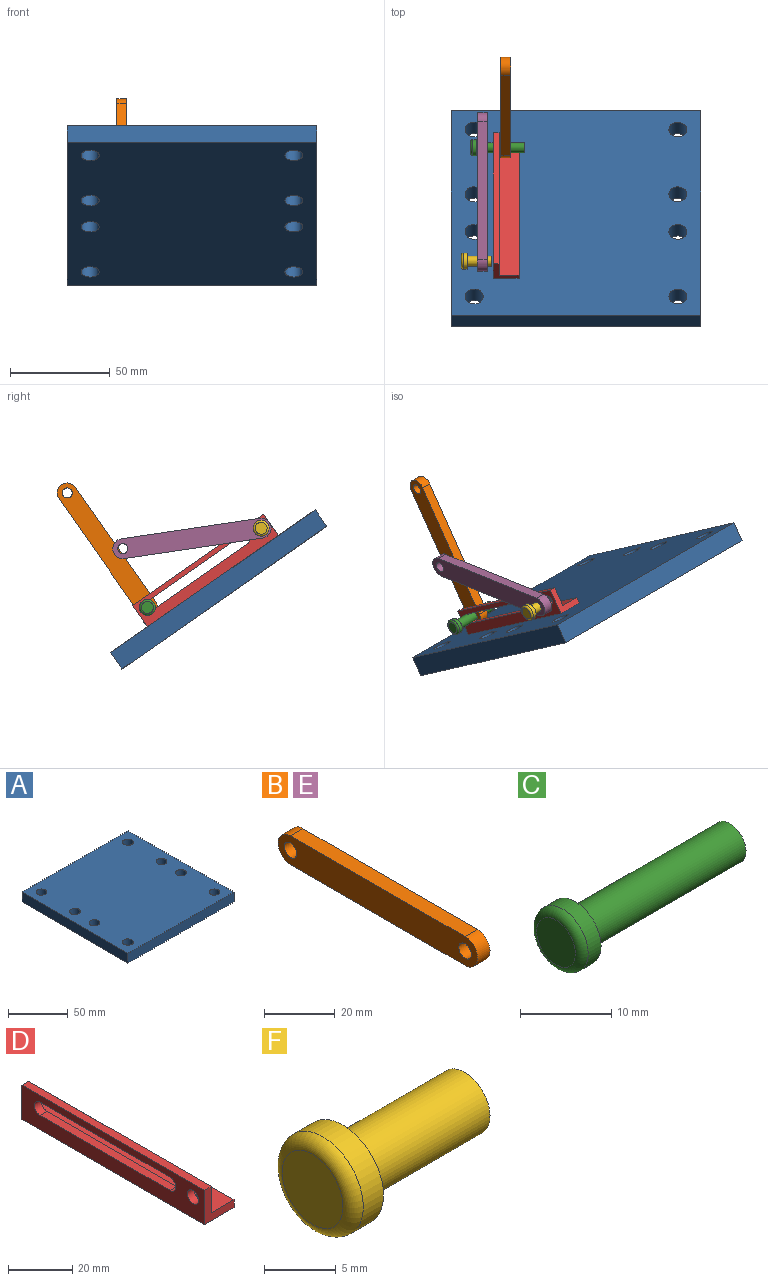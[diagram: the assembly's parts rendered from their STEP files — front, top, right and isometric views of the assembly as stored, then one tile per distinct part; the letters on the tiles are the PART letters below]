
ASSEMBLY  parts=6 mates=4
PART A: 14 faces, bbox 125x125x10 mm
  f0: plane 125x10mm, normal (0,-1,0), area 1250mm2, adj f1,f11,f12,f13
  f1: plane 125x10mm, normal (1,0,0), area 1250mm2, adj f0,f2,f12,f13
  f2: plane 125x10mm, normal (0,1,0), area 1250mm2, adj f1,f11,f12,f13
  f3: cylinder r=4.5mm len=10mm, axis (0,0,-1), area 282.7mm2, adj f12,f13
  f4: cylinder r=4.5mm len=10mm, axis (0,0,-1), area 282.7mm2, adj f12,f13
  f5: cylinder r=4.5mm len=10mm, axis (0,0,-1), area 282.7mm2, adj f12,f13
  f6: cylinder r=4.5mm len=10mm, axis (0,0,-1), area 282.7mm2, adj f12,f13
  f7: cylinder r=4.5mm len=10mm, axis (0,0,-1), area 282.7mm2, adj f12,f13
  f8: cylinder r=4.5mm len=10mm, axis (0,0,-1), area 282.7mm2, adj f12,f13
  f9: cylinder r=4.5mm len=10mm, axis (0,0,-1), area 282.7mm2, adj f12,f13
  f10: cylinder r=4.5mm len=10mm, axis (0,0,-1), area 282.7mm2, adj f12,f13
  f11: plane 125x10mm, normal (-1,0,0), area 1250mm2, adj f0,f2,f12,f13
  f12: plane 125x125mm, normal (0,0,1), area 15116.1mm2, adj f0,f1,f2,f3,f4,f5,f6,f7
  f13: plane 125x125mm, normal (0,0,-1), area 15116.1mm2, adj f0,f1,f2,f3,f4,f5,f6,f7
PART B: 8 faces, bbox 5x80x10 mm
  f0: plane 80x10mm, normal (1,0,0), area 739.3mm2, adj f2,f3,f4,f5,f6,f7
  f1: plane 80x10mm, normal (-1,0,0), area 739.3mm2, adj f2,f3,f4,f5,f6,f7
  f2: plane 70x5mm, normal (0,0,1), area 350mm2, adj f0,f1,f4,f5
  f3: plane 70x5mm, normal (0,0,-1), area 350mm2, adj f0,f1,f4,f5
  f4: cylinder r=5mm len=10mm, axis (-1,0,0), area 78.5mm2, adj f0,f1,f2,f3
  f5: cylinder r=5mm len=10mm, axis (-1,0,0), area 78.5mm2, adj f0,f1,f2,f3
  f6: cylinder r=2.5mm len=5mm, axis (-1,0,0), area 78.5mm2, adj f0,f1
  f7: cylinder r=2.5mm len=5mm, axis (-1,0,0), area 78.5mm2, adj f0,f1
PART C: 6 faces, bbox 27x8.7x8.7 mm
  f0: cylinder r=2.5mm len=24mm, axis (-1,0,0), area 377mm2, adj f1,f4
  f1: plane 5x5mm, normal (1,0,0), area 19.6mm2, adj f0
  f2: cylinder r=4mm len=8mm, axis (1,0,0), area 50.3mm2, adj f4,f5
  f3: plane 6x6mm, normal (-1,0,0), area 28.3mm2, adj f5
  f4: plane 8x8mm, normal (1,0,0), area 30.6mm2, adj f0,f2
  f5: torus R=3mm, axis (1,0,0), area 35.9mm2, adj f2,f3
PART D: 13 faces, bbox 13x80x13 mm
  f0: plane 80x13mm, normal (-1,0,0), area 715.7mm2, adj f4,f5,f6,f7,f8,f9,f10,f11
  f1: plane 80x10mm, normal (1,0,0), area 475.7mm2, adj f2,f4,f5,f7,f8,f9,f10,f11
  f2: plane 80x10mm, normal (0,0,1), area 800mm2, adj f1,f3,f4,f5
  f3: plane 80x3mm, normal (1,0,0), area 240mm2, adj f2,f4,f5,f6
  f4: plane 13x13mm, normal (0,1,0), area 69mm2, adj f0,f1,f2,f3,f6,f7
  f5: plane 13x13mm, normal (0,-1,0), area 69mm2, adj f0,f1,f2,f3,f6,f7
  f6: plane 80x13mm, normal (0,0,-1), area 1040mm2, adj f0,f3,f4,f5
  f7: plane 80x3mm, normal (0,0,1), area 240mm2, adj f0,f1,f4,f5
  f8: plane 57x3mm, normal (0,0,-1), area 171mm2, adj f0,f1,f9,f10
  f9: cylinder r=2.5mm len=5mm, axis (-1,0,0), area 23.6mm2, adj f0,f1,f8,f11
  f10: cylinder r=2.5mm len=5mm, axis (-1,0,0), area 23.6mm2, adj f0,f1,f8,f11
  f11: plane 57x3mm, normal (0,0,1), area 171mm2, adj f0,f1,f9,f10
  f12: cylinder r=2.5mm len=5mm, axis (-1,0,0), area 47.1mm2, adj f0,f1
PART E: same geometry as B
PART F: 6 faces, bbox 15x8.7x8.7 mm
  f0: cylinder r=2.5mm len=12mm, axis (-1,0,0), area 188.5mm2, adj f1,f4
  f1: plane 5x5mm, normal (1,0,0), area 19.6mm2, adj f0
  f2: cylinder r=4mm len=8mm, axis (1,0,0), area 50.3mm2, adj f4,f5
  f3: plane 6x6mm, normal (-1,0,0), area 28.3mm2, adj f5
  f4: plane 8x8mm, normal (1,0,0), area 30.6mm2, adj f0,f2
  f5: torus R=3mm, axis (1,0,0), area 35.9mm2, adj f2,f3
PLACE A rot(axis=(-1,0,0),34.9deg) t=(2.94,4.53,-54.44)mm
PLACE B rot(axis=(-1,0,0),125deg) t=(-32.24,59.03,-27.81)mm
PLACE C rot(axis=(-1,0,0),30deg) t=(-46.77,43.05,-59.35)mm
PLACE D rot(axis=(-1,0,0),34.9deg) t=(-32.06,11.97,-43.77)mm
PLACE E rot(axis=(-1,0,0),8.4deg) t=(-43.93,20,-29.73)mm
PLACE F rot(axis=(-1,0,0),34.9deg) t=(-51.51,-13.89,-19.65)mm
MATE slider F.f0 <-> D.f12  axis (-1,0,0) through (-51.51,-13.89,-19.65)mm
MATE cylindrical F.f0 <-> E.f4  axis (-1,0,0) through (-45.51,-13.89,-19.65)mm
MATE cylindrical C.f0 <-> B.f5  axis (-1,0,0) through (-34.77,43.05,-59.35)mm
MATE fastened D.f6 <-> A.f12  axis (0,-0.57,-0.82) through (-32.06,10.25,-46.23)mm
